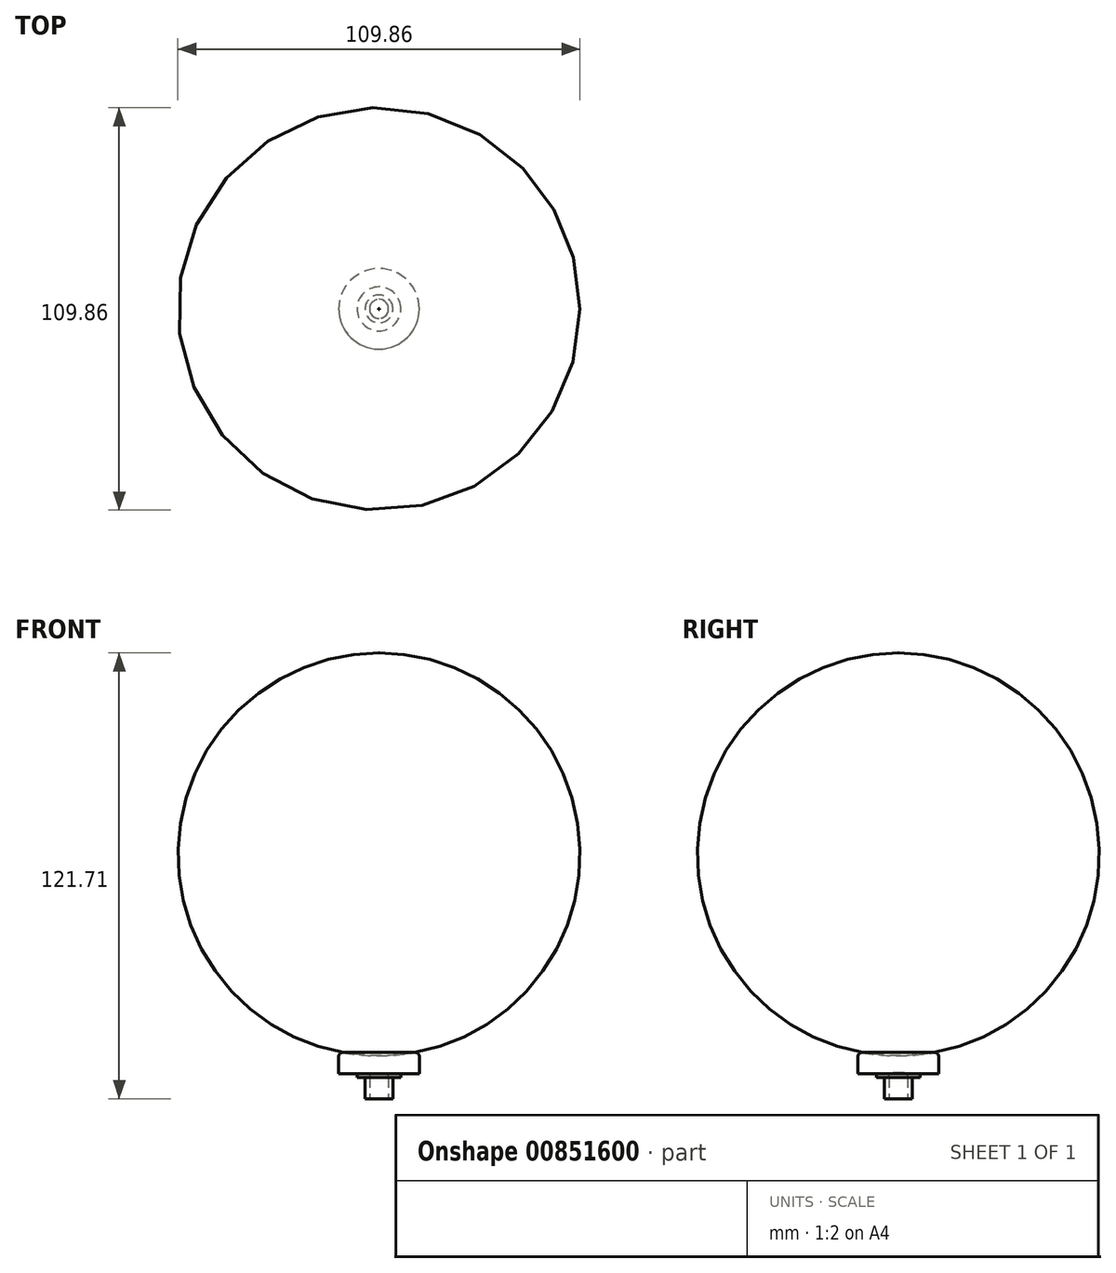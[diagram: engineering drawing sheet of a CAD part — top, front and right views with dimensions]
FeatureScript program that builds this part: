
annotation { "Feature Type Name" : "Feature", "Feature Type Description" : "" }
export const myFeature = defineFeature(function(context is Context, id is Id, definition is map)
    precondition{}
    {
        {
            var Q0;
            Q0=qCreatedBy(makeId("Front.planeOp"),FACE);
            var sketch = newSketch(context, id + "F0", { "sketchPlane" : qUnion([Q0])});
            skLineSegment(sketch, "E0", {"start": v(0, 18.8) * mm, "end": v(0, -20.61) * mm, "construction": true});
            skLineSegment(sketch, "E1", {"start": v(-3.8, -6.89) * mm, "end": v(-3.8, -0.09) * mm});
            skLineSegment(sketch, "E2", {"start": v(-3.8, -0.09) * mm, "end": v(-11, -0.09) * mm});
            skLineSegment(sketch, "E3", {"start": v(-11, -0.09) * mm, "end": v(-11, 5.91) * mm});
            skArc(sketch, "E4", {"start": v(-11, 5.91) * mm, "mid": v(-0.07, 4.82) * mm, "end": v(10.86, 5.91) * mm});
            skLineSegment(sketch, "E5", {"start": v(0, -6.89) * mm, "end": v(0, 4.82) * mm});
            skLineSegment(sketch, "E6", {"start": v(-3.8, -6.89) * mm, "end": v(0, -6.89) * mm});
            skLineSegment(sketch, "E7", {"start": v(-6, -0.09) * mm, "end": v(-6, -1.09) * mm});
            skLineSegment(sketch, "E8", {"start": v(-6, -1.09) * mm, "end": v(-3.8, -1.09) * mm});
            skSolve(sketch);
        }
        {
            var Q0;
            Q0 = qSketchRegion(id + "F0", true);
            var Q1;
            Q1=sQuery(id+"F0.wireOp",EDGE,"E5");
            revolve(context, id + "F1", {"surfaceOperationType" : NewSurfaceOperationType.NEW, "entities" : qUnion([Q0]), "axis" : qUnion([Q1]), "revolveType" : RevolveType.FULL});
        }
        {
            var Q0;
            Q0=makeQuery(id+"F1.opRevolve","SWEPT_EDGE",EDGE,{"disambiguationData":[OSD([sQuery(id+"F0.wireOp",EDGE,"E3"),sQuery(id+"F0.wireOp",EDGE,"E4")])]});
            fillet(context, id + "F2", {"entities" : qUnion([Q0]), "radius" : 1 * mm, "tangentPropagation" : true, "allowEdgeOverflow" : false});
        }
        {
            var Q0;
            Q0=makeQuery(id+"F1.opRevolve","SWEPT_FACE",FACE,{"disambiguationData":[OSD([sQuery(id+"F0.wireOp",EDGE,"E6")])]});
            var sketch = newSketch(context, id + "F3", { "sketchPlane" : qUnion([Q0])});
            skCircle(sketch, "E9.0.0", {"center": v(0, 0) * mm, "radius": 3.8 * mm});
            skCircle(sketch, "E10.0", {"center": v(0, 0) * mm, "radius": 2.6 * mm});
            skSolve(sketch);
        }
        {
            var Q0;
            Q0=makeQuery(id+"F3.imprint","IMPRINT",FACE,{"disambiguationData":[TD([[makeQuery(id+"F3.imprint","IMPRINT",EDGE,{"derivedFrom":sQuery(id+"F3.wireOp",EDGE,"E10.0")}),1.0]])]});
            extrude(context, id + "F4", {"entities" : qUnion([Q0]), "operationType" : NewBodyOperationType.REMOVE, "oppositeDirection" : true, "depth" : 7 * mm, "offsetDistance" : 25 * mm});
        }
        {
            var Q0;
            Q0=makeQuery(id+"F4.boolean.opBoolean","COPY",EDGE,{"derivedFrom":makeQuery(id+"F4.opExtrude","CAP_EDGE",EDGE,{"disambiguationData":[OSD([sQuery(id+"F3.wireOp",EDGE,"E10.0")])],"isStart":false})});
            fillet(context, id + "F5", {"entities" : qUnion([Q0]), "radius" : 1 * mm, "tangentPropagation" : true, "rho" : 0.5, "crossSection" : FilletCrossSection.CONIC, "allowEdgeOverflow" : false});
        }
    });
